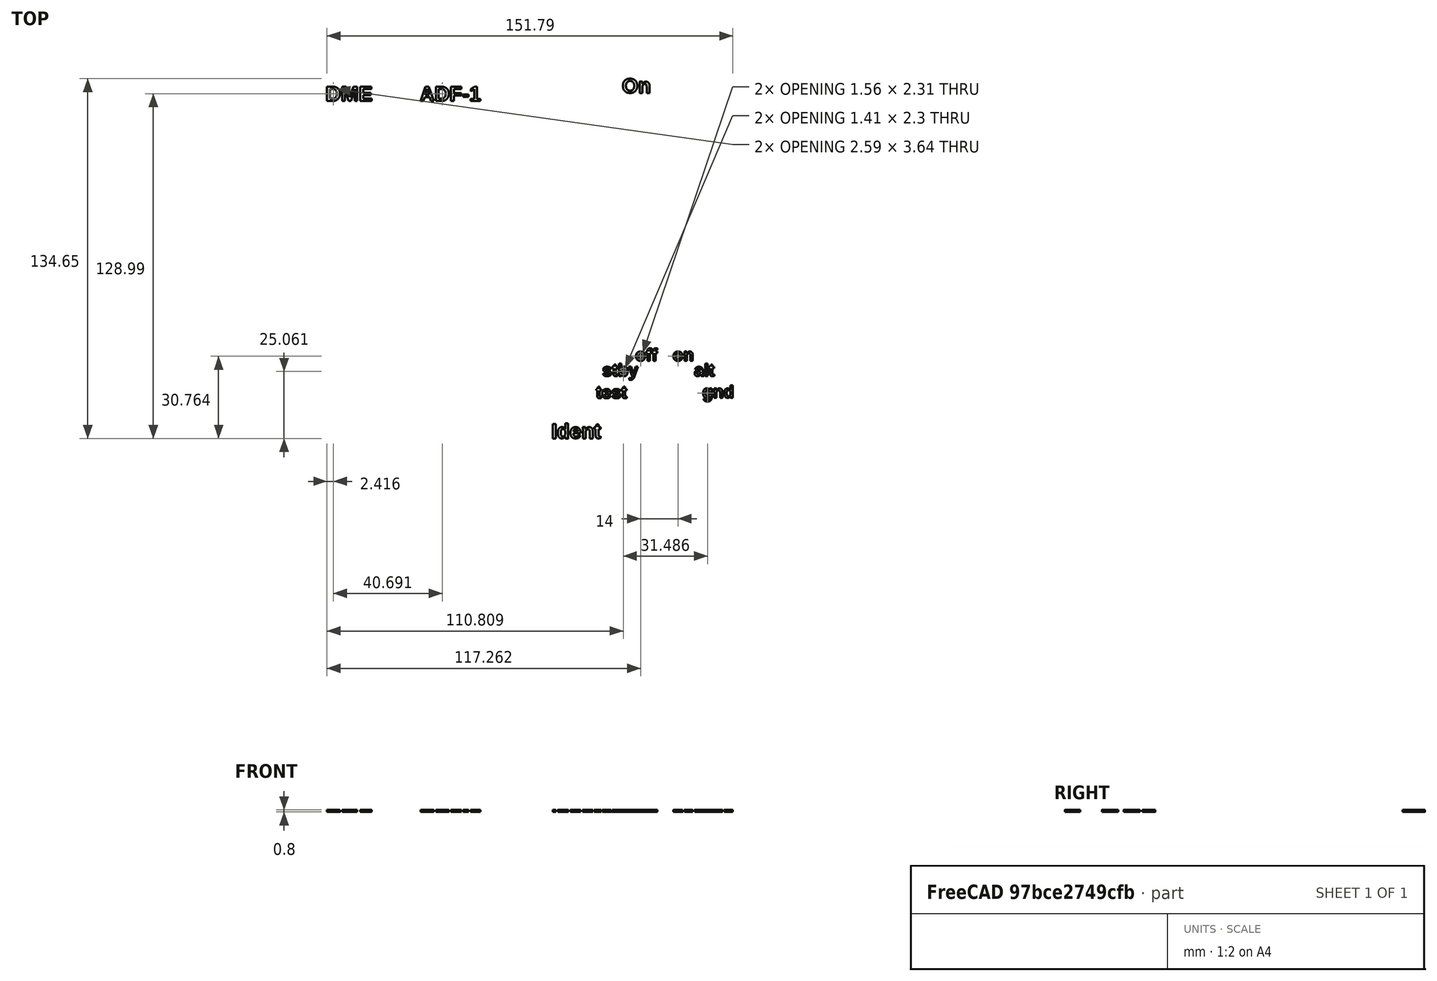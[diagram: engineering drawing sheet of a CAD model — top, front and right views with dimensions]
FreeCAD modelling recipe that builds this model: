
FCSTD DOCUMENT  (FreeCAD 0.17R13522 (Git))
Label: letras_derecha
License: CreativeCommons Attribution-ShareAlike
LicenseURL: http://creativecommons.org/licenses/by-sa/4.0/
objects: Part::Cut×17, Part::Box×10, Part::Feature×8
note: 35 computed .brp shape members not serialized (recipe doc carries the construction recipe); baked Part::Feature solids carry a one-line shape summary decoded from their .brp

FEATURE [Part::Feature] Cut001001001002003001008002002033001001001001001001001002001001002001042002001  label="Cut001001001002003001008002002033001001001001001001001002001001002001042003"
  shape: bbox 163 x 157.9 x 19 mm, 920 faces (baked)
FEATURE [Part::Box] Box  label="apoyo_fleje_lateral"
  AttacherType = Attacher::AttachEngine3D
  Height = 2
  Length = 1.5
  Placement = pos=(129.5,-4,-105) rot=(0,0,1;0rad)
  Width = 5
FEATURE [Part::Feature] Box001  label="apoyo_fleje_lateral001"
  Placement = pos=(129.5,148.85,-105) rot=(0,0,1;0rad)
  shape: bbox 1.5 x 5 x 2 mm, 6 faces (baked)
FEATURE [Part::Feature] Box001001  label="apoyo_fleje_lateral002"
  Placement = pos=(286.5,148.85,-105) rot=(0,0,1;0rad)
  shape: bbox 1.5 x 5 x 2 mm, 6 faces (baked)
FEATURE [Part::Feature] Box001001001  label="apoyo_fleje_lateral003"
  Placement = pos=(286.5,-4,-105) rot=(0,0,1;0rad)
  shape: bbox 1.5 x 5 x 2 mm, 6 faces (baked)
FEATURE [Part::Cut] Cut
  Base = -> Cut001001001002003001008002002033001001001001001001001002001001002001042002001
  Refine = true
  Tool = -> Box001001001
FEATURE [Part::Cut] Cut001001001002003001008002002033001001001001001001001002001001002001042002002
  Base = -> Cut
  Refine = true
  Tool = -> Box001001
FEATURE [Part::Cut] Cut001001001002003001008002002033001001001001001001001002001001002001042002003
  Base = -> Cut001001001002003001008002002033001001001001001001001002001001002001042002002
  Refine = true
  Tool = -> Box
FEATURE [Part::Cut] Cut001001001002003001008002002033001001001001001001001002001001002001042002004
  Base = -> Cut001001001002003001008002002033001001001001001001001002001001002001042002003
  Refine = true
  Tool = -> Box001
FEATURE [Part::Box] Box001001002  label="Cube"
  AttacherType = Attacher::AttachEngine3D
  Height = 2
  Length = 2
  Placement = pos=(203,-4,-105) rot=(0,0,1;0rad)
  Width = 5
FEATURE [Part::Feature] Box001001002001  label="Cube001"
  Placement = pos=(203,148.85,-105) rot=(0,0,1;0rad)
  shape: bbox 2 x 5 x 2 mm, 6 faces (baked)
FEATURE [Part::Cut] Cut001001001002003001008002002033001001001001001001001002001001002001042002005
  Base = -> Cut001001001002003001008002002033001001001001001001001002001001002001042002004
  Refine = true
  Tool = -> Box001001002001
FEATURE [Part::Cut] Cut001001001002003001008002002033001001001001001001001002001001002001042002006
  Base = -> Cut001001001002003001008002002033001001001001001001001002001001002001042002005
  Refine = true
  Tool = -> Box001001002
FEATURE [Part::Box] Box001001002002  label="Cube002"
  AttacherType = Attacher::AttachEngine3D
  Height = 10
  Length = 158
  Placement = pos=(130,-4,-103.9) rot=(0,0,1;0rad)
  Width = 157.85
FEATURE [Part::Cut] Cut001001001002003001008002002033001001001001001001001002001001002001042002007
  Base = -> Box001001002002
  Refine = true
  Tool = -> Cut001001001002003001008002002033001001001001001001001002001001002001042002006
FEATURE [Part::Box] Box001001002003  label="Cube003"
  AttacherType = Attacher::AttachEngine3D
  Height = 10
  Length = 158
  Placement = pos=(130,-4,-103.1) rot=(0,0,1;0rad)
  Width = 157.85
FEATURE [Part::Cut] Cut001001001002003001008002002033001001001001001001001002001001002001042002008
  Base = -> Cut001001001002003001008002002033001001001001001001001002001001002001042002007
  Refine = true
  Tool = -> Box001001002003
FEATURE [Part::Box] Box001001002004  label="Cube004"
  AttacherType = Attacher::AttachEngine3D
  Height = 10
  Length = 214
  Placement = pos=(0,-8,-108) rot=(0,0,1;0rad)
  Width = 136
FEATURE [Part::Cut] Cut001001001002003001008002002033001001001001001001001002001001002001042002009
  Base = -> Cut001001001002003001008002002033001001001001001001001002001001002001042002008
  Refine = true
  Tool = -> Box001001002004
FEATURE [Part::Box] Box001001002005  label="Cube005"
  AttacherType = Attacher::AttachEngine3D
  Height = 10
  Length = 200
  Placement = pos=(125,146,-107) rot=(0,0,1;0rad)
  Width = 10
FEATURE [Part::Cut] Cut001001001002003001008002002033001001001001001001001002001001002001042002010
  Base = -> Cut001001001002003001008002002033001001001001001001001002001001002001042002009
  Refine = true
  Tool = -> Box001001002005
FEATURE [Part::Box] Box001001002006  label="Cube006"
  AttacherType = Attacher::AttachEngine3D
  Height = 10
  Length = 10
  Placement = pos=(151,132,-107) rot=(0,0,1;0rad)
  Width = 10
FEATURE [Part::Feature] Box001001002006001  label="Cube007"
  Placement = pos=(191,132,-107) rot=(0,0,1;0rad)
  shape: bbox 10 x 10 x 10 mm, 6 faces (baked)
FEATURE [Part::Feature] Box001001002006001001  label="Cube008"
  Placement = pos=(256,132,-107) rot=(0,0,1;0rad)
  shape: bbox 10 x 10 x 10 mm, 6 faces (baked)
FEATURE [Part::Cut] Cut001001001002003001008002002033001001001001001001001002001001002001042002011
  Base = -> Cut001001001002003001008002002033001001001001001001001002001001002001042002010
  Refine = true
  Tool = -> Box001001002006001001
FEATURE [Part::Cut] Cut001001001002003001008002002033001001001001001001001002001001002001042002012
  Base = -> Cut001001001002003001008002002033001001001001001001001002001001002001042002011
  Refine = true
  Tool = -> Box001001002006
FEATURE [Part::Cut] Cut001001001002003001008002002033001001001001001001001002001001002001042002013
  Base = -> Cut001001001002003001008002002033001001001001001001001002001001002001042002012
  Refine = true
  Tool = -> Box001001002006001
FEATURE [Part::Box] Box001001002006001002  label="Cube009"
  AttacherType = Attacher::AttachEngine3D
  Height = 10
  Length = 22
  Placement = pos=(250,50,-107) rot=(0,0,1;0rad)
  Width = 64
FEATURE [Part::Cut] Cut001001001002003001008002002033001001001001001001001002001001002001042002014
  Base = -> Cut001001001002003001008002002033001001001001001001001002001001002001042002013
  Refine = true
  Tool = -> Box001001002006001002
FEATURE [Part::Box] Box001001002006001003  label="Cube010"
  AttacherType = Attacher::AttachEngine3D
  Height = 10
  Length = 13
  Placement = pos=(219,12,-107) rot=(0,0,1;0rad)
  Width = 13
FEATURE [Part::Feature] Box001001002006001003001  label="Cube011"
  Placement = pos=(254,12,-107) rot=(0,0,1;0rad)
  shape: bbox 13 x 13 x 10 mm, 6 faces (baked)
FEATURE [Part::Cut] Cut001001001002003001008002002033001001001001001001001002001001002001042002015
  Base = -> Cut001001001002003001008002002033001001001001001001001002001001002001042002014
  Refine = true
  Tool = -> Box001001002006001003001
FEATURE [Part::Cut] Cut001001001002003001008002002033001001001001001001001002001001002001042002016
  Base = -> Cut001001001002003001008002002033001001001001001001001002001001002001042002015
  Refine = true
  Tool = -> Box001001002006001003
FEATURE [Part::Box] Box001001002006001003002  label="Cube012"
  AttacherType = Attacher::AttachEngine3D
  Height = 10
  Length = 10
  Placement = pos=(283,-7,-107) rot=(0,0,1;0rad)
  Width = 10
FEATURE [Part::Cut] Cut001001001002003001008002002033001001001001001001001002001001002001042002017  label="letras_derecha"
  Base = -> Cut001001001002003001008002002033001001001001001001001002001001002001042002016
  Refine = true
  Tool = -> Box001001002006001003002
